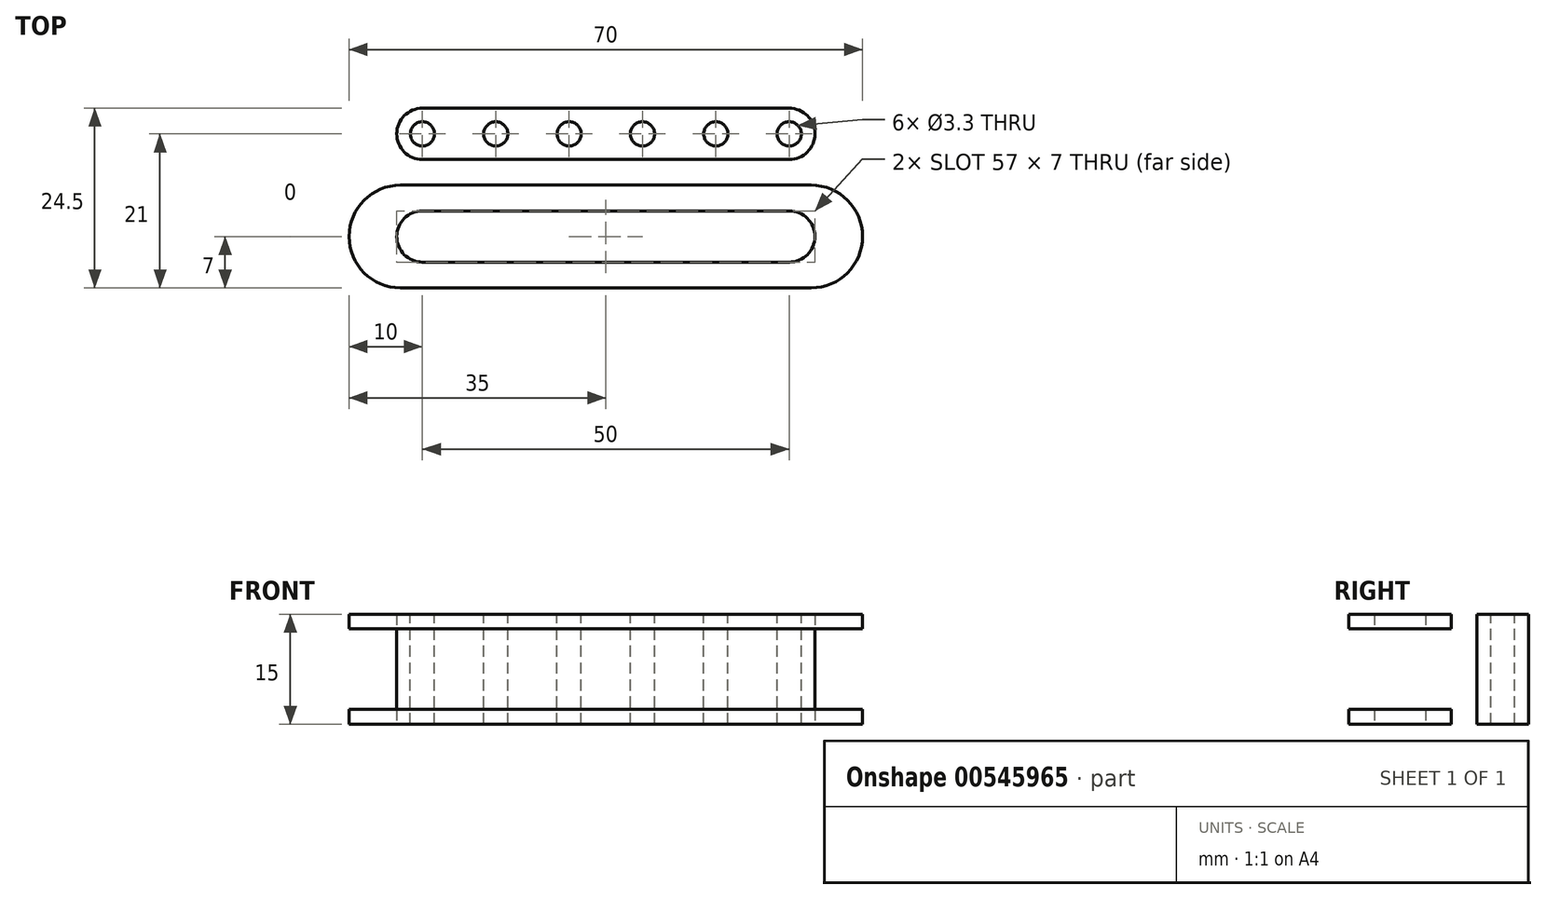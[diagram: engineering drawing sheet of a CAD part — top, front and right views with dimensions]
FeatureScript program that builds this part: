
annotation { "Feature Type Name" : "Feature", "Feature Type Description" : "" }
export const myFeature = defineFeature(function(context is Context, id is Id, definition is map)
    precondition{}
    {
        {
            var Q0;
            Q0=qCreatedBy(makeId("Top.planeOp"),FACE);
            var sketch = newSketch(context, id + "F0", { "sketchPlane" : qUnion([Q0])});
            skLineSegment(sketch, "E0.bottom", {"start": v(28, -7) * mm, "end": v(-28, -7) * mm});
            skLineSegment(sketch, "E0.top", {"start": v(28, 7) * mm, "end": v(-28, 7) * mm});
            skLineSegment(sketch, "E0.left", {"start": v(35, 0) * mm, "end": v(35, 0) * mm});
            skLineSegment(sketch, "E0.right", {"start": v(-35, 0) * mm, "end": v(-35, 0) * mm});
            skPoint(sketch, "E0.middle", {"position": v(0, 0) * mm});
            skPoint(sketch, "E1.visualSharp", {"position": v(-35, 7) * mm});
            skArc(sketch, "E1.filletArc", {"start": v(-28, 7) * mm, "mid": v(-32.95, 4.95) * mm, "end": v(-35, 0) * mm});
            skPoint(sketch, "E2.visualSharp", {"position": v(-35, -7) * mm});
            skArc(sketch, "E2.filletArc", {"start": v(-35, 0) * mm, "mid": v(-32.95, -4.95) * mm, "end": v(-28, -7) * mm});
            skPoint(sketch, "E3.visualSharp", {"position": v(35, 7) * mm});
            skArc(sketch, "E3.filletArc", {"start": v(35, 0) * mm, "mid": v(32.95, 4.95) * mm, "end": v(28, 7) * mm});
            skPoint(sketch, "E4.visualSharp", {"position": v(35, -7) * mm});
            skArc(sketch, "E4.filletArc", {"start": v(28, -7) * mm, "mid": v(32.95, -4.95) * mm, "end": v(35, 0) * mm});
            skPoint(sketch, "E5", {"position": v(15, 0) * mm});
            skPoint(sketch, "E6", {"position": v(5, 0) * mm});
            skPoint(sketch, "E7", {"position": v(-5, 0) * mm});
            skPoint(sketch, "E8", {"position": v(-15, 0) * mm});
            skPoint(sketch, "E9", {"position": v(-25, 0) * mm});
            skPoint(sketch, "E10", {"position": v(25, 0) * mm});
            skLineSegment(sketch, "E11.bottom", {"start": v(25, 3.5) * mm, "end": v(-25, 3.5) * mm});
            skLineSegment(sketch, "E11.top", {"start": v(25, -3.5) * mm, "end": v(-25, -3.5) * mm});
            skLineSegment(sketch, "E11.left", {"start": v(28.5, 0) * mm, "end": v(28.5, 0) * mm});
            skLineSegment(sketch, "E11.right", {"start": v(-28.5, 0) * mm, "end": v(-28.5, 0) * mm});
            skPoint(sketch, "E12.visualSharp", {"position": v(-28.5, 3.5) * mm});
            skArc(sketch, "E12.filletArc", {"start": v(-25, 3.5) * mm, "mid": v(-27.47, 2.47) * mm, "end": v(-28.5, 0) * mm});
            skPoint(sketch, "E13.visualSharp", {"position": v(-28.5, -3.5) * mm});
            skArc(sketch, "E13.filletArc", {"start": v(-28.5, 0) * mm, "mid": v(-27.47, -2.47) * mm, "end": v(-25, -3.5) * mm});
            skPoint(sketch, "E14.visualSharp", {"position": v(28.5, -3.5) * mm});
            skArc(sketch, "E14.filletArc", {"start": v(25, -3.5) * mm, "mid": v(27.47, -2.47) * mm, "end": v(28.5, 0) * mm});
            skPoint(sketch, "E15.visualSharp", {"position": v(28.5, 3.5) * mm});
            skArc(sketch, "E15.filletArc", {"start": v(28.5, 0) * mm, "mid": v(27.47, 2.47) * mm, "end": v(25, 3.5) * mm});
            skSolve(sketch);
        }
        {
            var Q0;
            Q0=makeQuery(id+"F0.imprint","IMPRINT",FACE,{"disambiguationData":[TD([[makeQuery(id+"F0.imprint","IMPRINT",EDGE,{"derivedFrom":sQuery(id+"F0.wireOp",EDGE,"E11.bottom")}),1.0]])]});
            extrude(context, id + "F1", {"entities" : qUnion([Q0]), "depth" : 15 * mm, "offsetDistance" : 25 * mm});
        }
        {
            var Q0;
            Q0=qSketchRegion(id+"F0",true);
            extrude(context, id + "F2", {"entities" : qUnion([Q0]), "depth" : 2 * mm, "offsetDistance" : 25 * mm});
        }
        {
            var Q0;
            Q0=makeQuery(id+"F2.opExtrude","SWEPT_BODY",BODY,{"disambiguationData":[OSD([sQuery(id+"F0.wireOp",EDGE,"E0.bottom"),sQuery(id+"F0.wireOp",EDGE,"E0.top"),sQuery(id+"F0.wireOp",EDGE,"E1.filletArc"),sQuery(id+"F0.wireOp",EDGE,"E2.filletArc"),sQuery(id+"F0.wireOp",EDGE,"E3.filletArc"),sQuery(id+"F0.wireOp",EDGE,"E4.filletArc"),sQuery(id+"F0.wireOp",EDGE,"E11.bottom"),sQuery(id+"F0.wireOp",EDGE,"E11.top"),sQuery(id+"F0.wireOp",EDGE,"E12.filletArc"),sQuery(id+"F0.wireOp",EDGE,"E13.filletArc"),sQuery(id+"F0.wireOp",EDGE,"E14.filletArc"),sQuery(id+"F0.wireOp",EDGE,"E15.filletArc")])]});
            var Q1;
            Q1=makeQuery(id+"F1.opExtrude","SWEPT_EDGE",EDGE,{"disambiguationData":[OSD([sQuery(id+"F0.wireOp",EDGE,"E11.bottom"),sQuery(id+"F0.wireOp",EDGE,"E12.filletArc")])]});
            transform(context, id + "F3", {"entities" : qUnion([Q0]), "transformType" : TransformType.TRANSLATION_DISTANCE, "transformDirection" : qUnion([Q1]), "distance" : 13 * mm, "oppositeDirection" : true, "makeCopy" : true});
        }
        {
            var Q0;
            Q0=sQuery(id+"F0.wireOp",VERTEX,"E9");
            var Q1;
            Q1=sQuery(id+"F0.wireOp",VERTEX,"E8");
            var Q2;
            Q2=sQuery(id+"F0.wireOp",VERTEX,"E7");
            var Q3;
            Q3=sQuery(id+"F0.wireOp",VERTEX,"E6");
            var Q4;
            Q4=sQuery(id+"F0.wireOp",VERTEX,"E5");
            var Q5;
            Q5=sQuery(id+"F0.wireOp",VERTEX,"E10");
            var Q6;
            Q6=makeQuery(id+"F1.opExtrude","SWEPT_BODY",BODY,{"disambiguationData":[OSD([sQuery(id+"F0.wireOp",EDGE,"E11.bottom"),sQuery(id+"F0.wireOp",EDGE,"E11.top"),sQuery(id+"F0.wireOp",EDGE,"E12.filletArc"),sQuery(id+"F0.wireOp",EDGE,"E13.filletArc"),sQuery(id+"F0.wireOp",EDGE,"E14.filletArc"),sQuery(id+"F0.wireOp",EDGE,"E15.filletArc")])]});
            hole(context, id + "F4", {"style" : HoleStyle.SIMPLE, "endStyle" : HoleEndStyle.THROUGH, "oppositeDirection" : true, "standardTappedOrClearance" : lookupTablePath({ "standard" : "ISO", "engagement" : "75%", "pitch" : "0.7 mm", "size" : "M4", "type" : "Tapped" }), "standardBlindInLast" : lookupTablePath({ "standard" : "ISO", "engagement" : "75%", "pitch" : "0.7 mm", "size" : "M4", "type" : "Tapped" }), "holeDiameter" : 3.3 * mm, "showTappedDepth" : true, "isTappedThrough" : true, "tappedDepth" : 12 * mm, "tapClearance" : 3, "startFromSketch" : true, "locations" : qUnion([Q0, Q1, Q2, Q3, Q4, Q5]), "scope" : qUnion([Q6]), "majorDiameter" : 4 * mm});
        }
        {
            var Q0;
            Q0=makeQuery(id+"F1.opExtrude","SWEPT_BODY",BODY,{"disambiguationData":[OSD([sQuery(id+"F0.wireOp",EDGE,"E11.bottom"),sQuery(id+"F0.wireOp",EDGE,"E11.top"),sQuery(id+"F0.wireOp",EDGE,"E12.filletArc"),sQuery(id+"F0.wireOp",EDGE,"E13.filletArc"),sQuery(id+"F0.wireOp",EDGE,"E14.filletArc"),sQuery(id+"F0.wireOp",EDGE,"E15.filletArc")])]});
            var Q1;
            Q1=makeQuery(id+"F2.opExtrude","CAP_EDGE",EDGE,{"disambiguationData":[OSD([sQuery(id+"F0.wireOp",EDGE,"E0.top")])],"isStart":false});
            transform(context, id + "F5", {"entities" : qUnion([Q0]), "transformType" : TransformType.ROTATION, "transformAxis" : qUnion([Q1]), "angle" : 180 * degree, "makeCopy" : false});
        }
        {
            var Q0;
            Q0=makeQuery(id+"F1.opExtrude","SWEPT_BODY",BODY,{"disambiguationData":[OSD([sQuery(id+"F0.wireOp",EDGE,"E11.bottom"),sQuery(id+"F0.wireOp",EDGE,"E11.top"),sQuery(id+"F0.wireOp",EDGE,"E12.filletArc"),sQuery(id+"F0.wireOp",EDGE,"E13.filletArc"),sQuery(id+"F0.wireOp",EDGE,"E14.filletArc"),sQuery(id+"F0.wireOp",EDGE,"E15.filletArc")])]});
            var Q1;
            Q1=makeQuery(id+"F1.opExtrude","SWEPT_EDGE",EDGE,{"disambiguationData":[OSD([sQuery(id+"F0.wireOp",EDGE,"E11.bottom"),sQuery(id+"F0.wireOp",EDGE,"E12.filletArc")])]});
            transform(context, id + "F6", {"entities" : qUnion([Q0]), "transformType" : TransformType.TRANSLATION_DISTANCE, "transformDirection" : qUnion([Q1]), "distance" : 11 * mm, "makeCopy" : false});
        }
        {
            var Q0;
            Q0=qCreatedBy(makeId("Right.planeOp"),FACE);
            var sketch = newSketch(context, id + "F7", { "sketchPlane" : qUnion([Q0])});
            skLineSegment(sketch, "E16.right", {"start": v(-1.68, 0) * mm, "end": v(-1.68, 16) * mm});
            skLineSegment(sketch, "E17.left", {"start": v(-3.53, 20) * mm, "end": v(-3.53, 16) * mm});
            skLineSegment(sketch, "E18", {"start": v(-0.03, 16) * mm, "end": v(-0.03, 0) * mm});
            skLineSegment(sketch, "E19", {"start": v(-1.68, 0) * mm, "end": v(-0.03, 0) * mm});
            skLineSegment(sketch, "E20", {"start": v(-0.03, 16) * mm, "end": v(-0.03, 20) * mm});
            skLineSegment(sketch, "E21", {"start": v(-1.68, 16) * mm, "end": v(-3.53, 16) * mm});
            skLineSegment(sketch, "E22", {"start": v(-3.53, 20) * mm, "end": v(-0.03, 20) * mm});
            skSolve(sketch);
        }
        {
            var Q0;
            Q0=makeQuery(id+"F7.imprint","IMPRINT",FACE,{"disambiguationData":[TD([[makeQuery(id+"F7.imprint","IMPRINT",EDGE,{"derivedFrom":sQuery(id+"F7.wireOp",EDGE,"E16.right")}),-1.0]])]});
            var Q1;
            Q1=sQuery(id+"F7.wireOp",EDGE,"E18");
            revolve(context, id + "F8", {"entities" : qUnion([Q0]), "axis" : qUnion([Q1]), "revolveType" : RevolveType.FULL});
        }
        {
            var Q0;
            Q0=makeQuery(id+"F8.opRevolve","SWEPT_BODY",BODY,{"disambiguationData":[OSD([sQuery(id+"F7.wireOp",EDGE,"E16.right"),sQuery(id+"F7.wireOp",EDGE,"E17.left"),sQuery(id+"F7.wireOp",EDGE,"E18"),sQuery(id+"F7.wireOp",EDGE,"E19"),sQuery(id+"F7.wireOp",EDGE,"E20"),sQuery(id+"F7.wireOp",EDGE,"E21"),sQuery(id+"F7.wireOp",EDGE,"E22")])]});
            deleteBodies(context, id + "F9", {"entities" : qUnion([Q0])});
        }
    });
